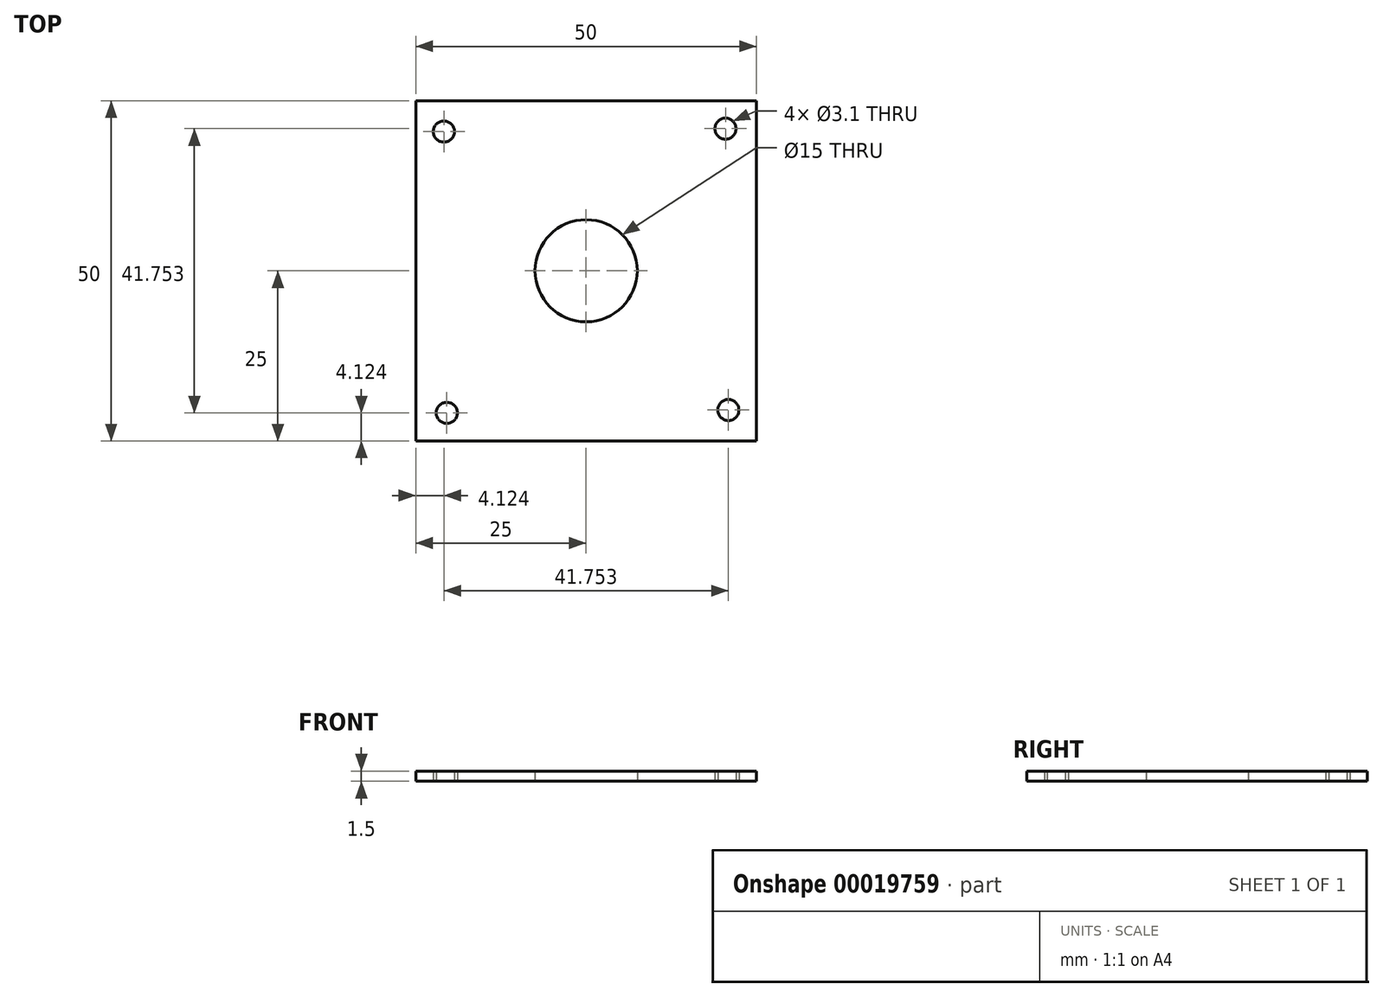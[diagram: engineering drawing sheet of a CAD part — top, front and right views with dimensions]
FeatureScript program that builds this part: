
annotation { "Feature Type Name" : "Feature", "Feature Type Description" : "" }
export const myFeature = defineFeature(function(context is Context, id is Id, definition is map)
    precondition{}
    {
        {
            var Q0;
            Q0=qCreatedBy(makeId("Top.planeOp"),FACE);
            var sketch = newSketch(context, id + "F0", { "sketchPlane" : qUnion([Q0])});
            skLineSegment(sketch, "E0.rect.bottom", {"start": v(25, -25) * mm, "end": v(-25, -25) * mm});
            skLineSegment(sketch, "E0.rect.top", {"start": v(25, 25) * mm, "end": v(-25, 25) * mm});
            skLineSegment(sketch, "E0.rect.left", {"start": v(25, -25) * mm, "end": v(25, 25) * mm});
            skLineSegment(sketch, "E0.rect.right", {"start": v(-25, -25) * mm, "end": v(-25, 25) * mm});
            skPoint(sketch, "E0.rect.middle", {"position": v(0, 0) * mm});
            skCircle(sketch, "E1", {"center": v(0, 0) * mm, "radius": 7.5 * mm});
            skCircle(sketch, "E2", {"center": v(-20.88, 20.45) * mm, "radius": 1.55 * mm});
            skCircle(sketch, "E3.1.0", {"center": v(-20.45, -20.88) * mm, "radius": 1.55 * mm});
            skCircle(sketch, "E3.2.0", {"center": v(20.88, -20.45) * mm, "radius": 1.55 * mm});
            skCircle(sketch, "E3.3.0", {"center": v(20.45, 20.88) * mm, "radius": 1.55 * mm});
            skSolve(sketch);
        }
        {
            var Q0;
            Q0=makeQuery(id+"F0.imprint","IMPRINT",FACE,{"disambiguationData":[TD([[makeQuery(id+"F0.imprint","IMPRINT",EDGE,{"derivedFrom":sQuery(id+"F0.wireOp",EDGE,"E0.rect.bottom")}),-1.0]])]});
            extrude(context, id + "F1", {"entities" : qUnion([Q0]), "depth" : 1.5 * mm});
        }
    });
